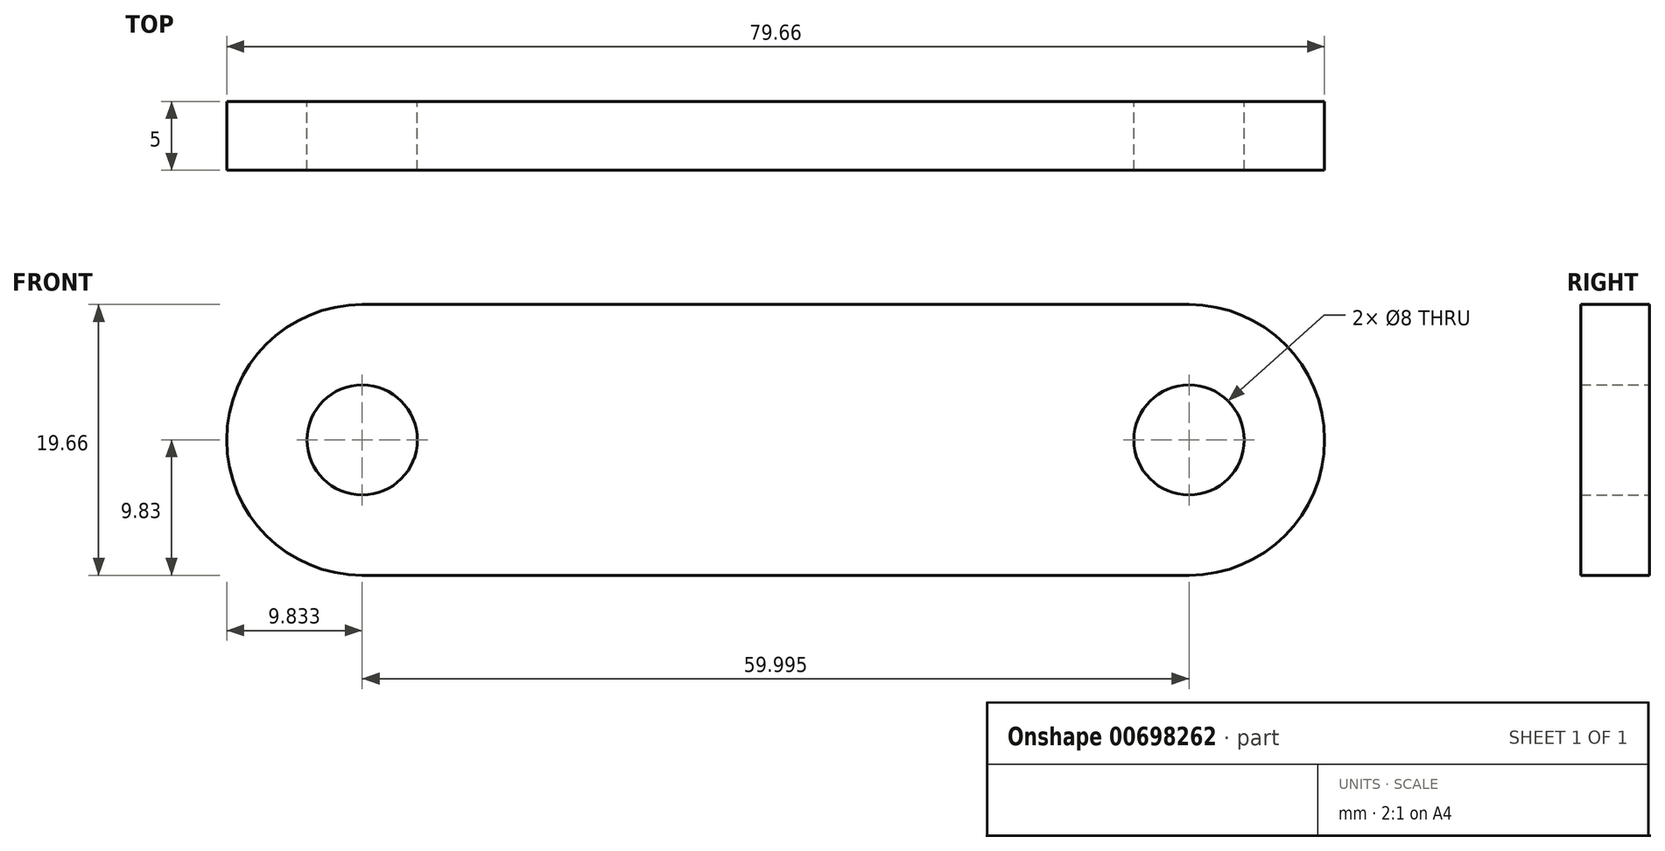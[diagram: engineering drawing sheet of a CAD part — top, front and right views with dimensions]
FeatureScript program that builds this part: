
annotation { "Feature Type Name" : "Feature", "Feature Type Description" : "" }
export const myFeature = defineFeature(function(context is Context, id is Id, definition is map)
    precondition{}
    {
        {
            var Q0;
            Q0=qCreatedBy(makeId("Front.planeOp"),FACE);
            var sketch = newSketch(context, id + "F0", { "sketchPlane" : qUnion([Q0])});
            skLineSegment(sketch, "E0", {"start": v(0, 0) * mm, "end": v(-30, 0) * mm});
            skArc(sketch, "E1", {"start": v(-30, 9.83) * mm, "mid": v(-39.83, 0) * mm, "end": v(-30, -9.83) * mm});
            skLineSegment(sketch, "E2", {"start": v(0, 9.83) * mm, "end": v(-30, 9.83) * mm});
            skLineSegment(sketch, "E3", {"start": v(0, -9.83) * mm, "end": v(-30, -9.83) * mm});
            skLineSegment(sketch, "E4.MirrorCS", {"start": v(0, 9.83) * mm, "end": v(30, 9.83) * mm});
            skArc(sketch, "E5.MirrorCS", {"start": v(30, 9.83) * mm, "mid": v(39.83, 0) * mm, "end": v(30, -9.83) * mm});
            skLineSegment(sketch, "E6.MirrorCS", {"start": v(0, -9.83) * mm, "end": v(30, -9.83) * mm});
            skCircle(sketch, "E7", {"center": v(-30, 0) * mm, "radius": 4 * mm});
            skCircle(sketch, "E8.MirrorC", {"center": v(30, 0) * mm, "radius": 4 * mm});
            skSolve(sketch);
        }
        {
            var Q0;
            Q0=makeQuery(id+"F0.imprint","IMPRINT",FACE,{"disambiguationData":[TD([[makeQuery(id+"F0.imprint","IMPRINT",EDGE,{"derivedFrom":sQuery(id+"F0.wireOp",EDGE,"E1")}),1.0]])]});
            extrude(context, id + "F1", {"entities" : qUnion([Q0]), "endBound" : BoundingType.SYMMETRIC, "depth" : 5 * mm, "offsetDistance" : 25.4 * mm});
        }
    });
